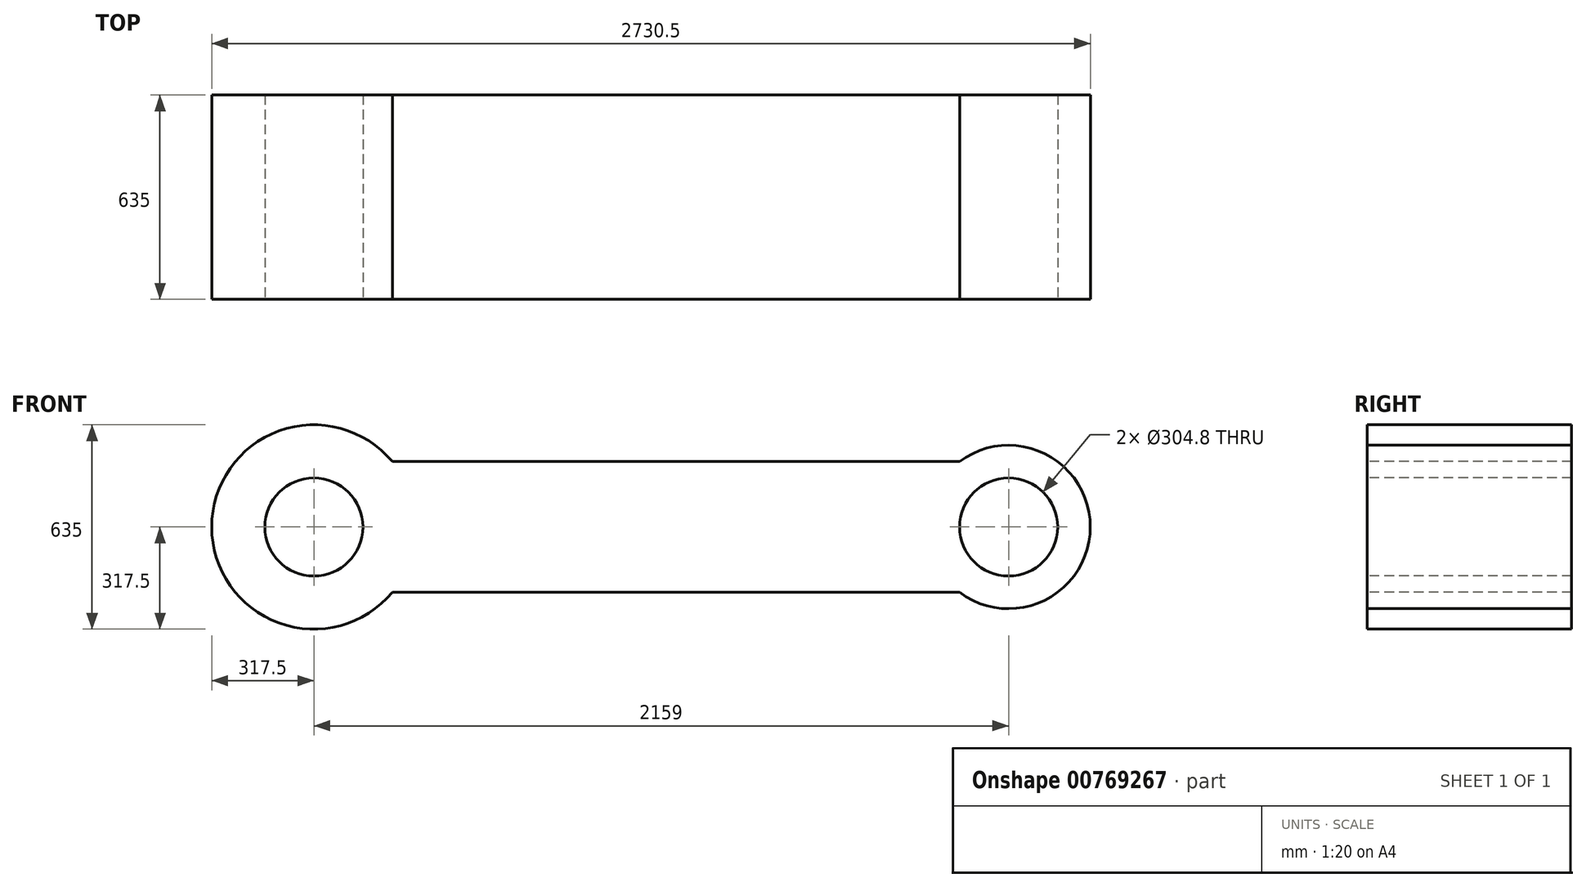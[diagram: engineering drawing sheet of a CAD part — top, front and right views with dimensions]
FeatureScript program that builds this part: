
annotation { "Feature Type Name" : "Feature", "Feature Type Description" : "" }
export const myFeature = defineFeature(function(context is Context, id is Id, definition is map)
    precondition{}
    {
        {
            var Q0;
            Q0=qCreatedBy(makeId("Front.planeOp"),FACE);
            var sketch = newSketch(context, id + "F0", { "sketchPlane" : qUnion([Q0])});
            skCircle(sketch, "E0", {"center": v(0, 0) * mm, "radius": 317.5 * mm});
            skCircle(sketch, "E1", {"center": v(2159, 0) * mm, "radius": 254 * mm});
            skLineSegment(sketch, "E2", {"start": v(243.96, 203.2) * mm, "end": v(2006.6, 203.2) * mm});
            skLineSegment(sketch, "E3.MirrorCS", {"start": v(243.96, -203.2) * mm, "end": v(2006.6, -203.2) * mm});
            skCircle(sketch, "E4", {"center": v(0, 0) * mm, "radius": 152.4 * mm});
            skCircle(sketch, "E5", {"center": v(2159, 0) * mm, "radius": 152.4 * mm});
            skSolve(sketch);
        }
        {
            var Q0;
            Q0=makeQuery(id+"F0.imprint","IMPRINT",FACE,{"disambiguationData":[TD([[makeQuery(id+"F0.imprint","IMPRINT",EDGE,{"derivedFrom":sQuery(id+"F0.wireOp",EDGE,"E4")}),-1.0]])]});
            var Q1;
            {var subQ0=sQuery(id+"F0.wireOp",EDGE,"E2");Q1=makeQuery(id+"F0.imprint","IMPRINT",FACE,{"disambiguationData":[TD([[makeQuery(id+"F0.imprint","IMPRINT",EDGE,{"derivedFrom":subQ0}),-1.0]])]});}
            var Q2;
            Q2=makeQuery(id+"F0.imprint","IMPRINT",FACE,{"disambiguationData":[TD([[makeQuery(id+"F0.imprint","IMPRINT",EDGE,{"derivedFrom":sQuery(id+"F0.wireOp",EDGE,"E5")}),-1.0]])]});
            var Q3;
            Q3=sQuery(id+"F0.wireOp",EDGE,"E0");
            var Q4;
            Q4=sQuery(id+"F0.wireOp",EDGE,"E2");
            var Q5;
            Q5=sQuery(id+"F0.wireOp",EDGE,"E3.MirrorCS");
            var Q6;
            Q6=sQuery(id+"F0.wireOp",EDGE,"E1");
            var Q7;
            Q7=sQuery(id+"F0.wireOp",EDGE,"E5");
            extrude(context, id + "F1", {"entities" : qUnion([Q0, Q1, Q2]), "surfaceEntities" : qUnion([Q3, Q4, Q5, Q6, Q7]), "oppositeDirection" : true, "depth" : 635 * mm, "offsetDistance" : 25.4 * mm});
        }
    });
